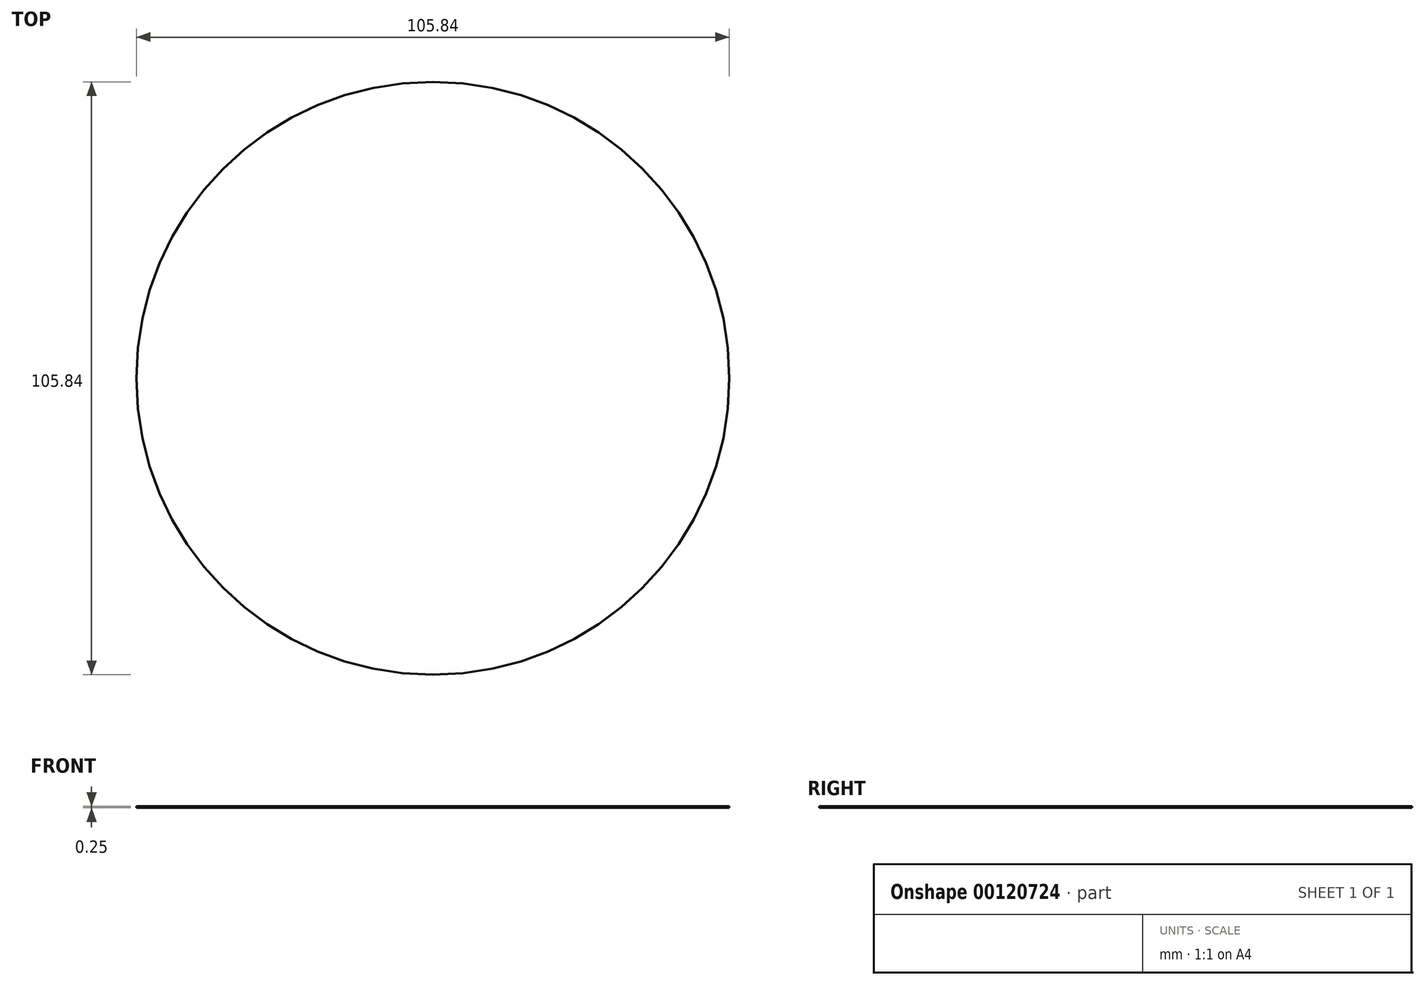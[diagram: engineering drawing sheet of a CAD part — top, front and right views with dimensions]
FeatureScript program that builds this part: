
annotation { "Feature Type Name" : "Feature", "Feature Type Description" : "" }
export const myFeature = defineFeature(function(context is Context, id is Id, definition is map)
    precondition{}
    {
        {
            assignVariable(context, id + "F0", {"name" : "thickness", "anyValue" : .25});
        }
        {
            var Q0;
            Q0=qCreatedBy(makeId("Top.planeOp"),FACE);
            var sketch = newSketch(context, id + "F1", { "sketchPlane" : qUnion([Q0])});
            skCircle(sketch, "E0", {"center": v(0, 0) * mm, "radius": 52.92 * mm});
            skSolve(sketch);
        }
        {
            var Q0;
            Q0 = qSketchRegion(id + "F1", true);
            extrude(context, id + "F2", {"entities" : qUnion([Q0]), "depth" : (getVariable(context, 'thickness')) * mm});
        }
    });
